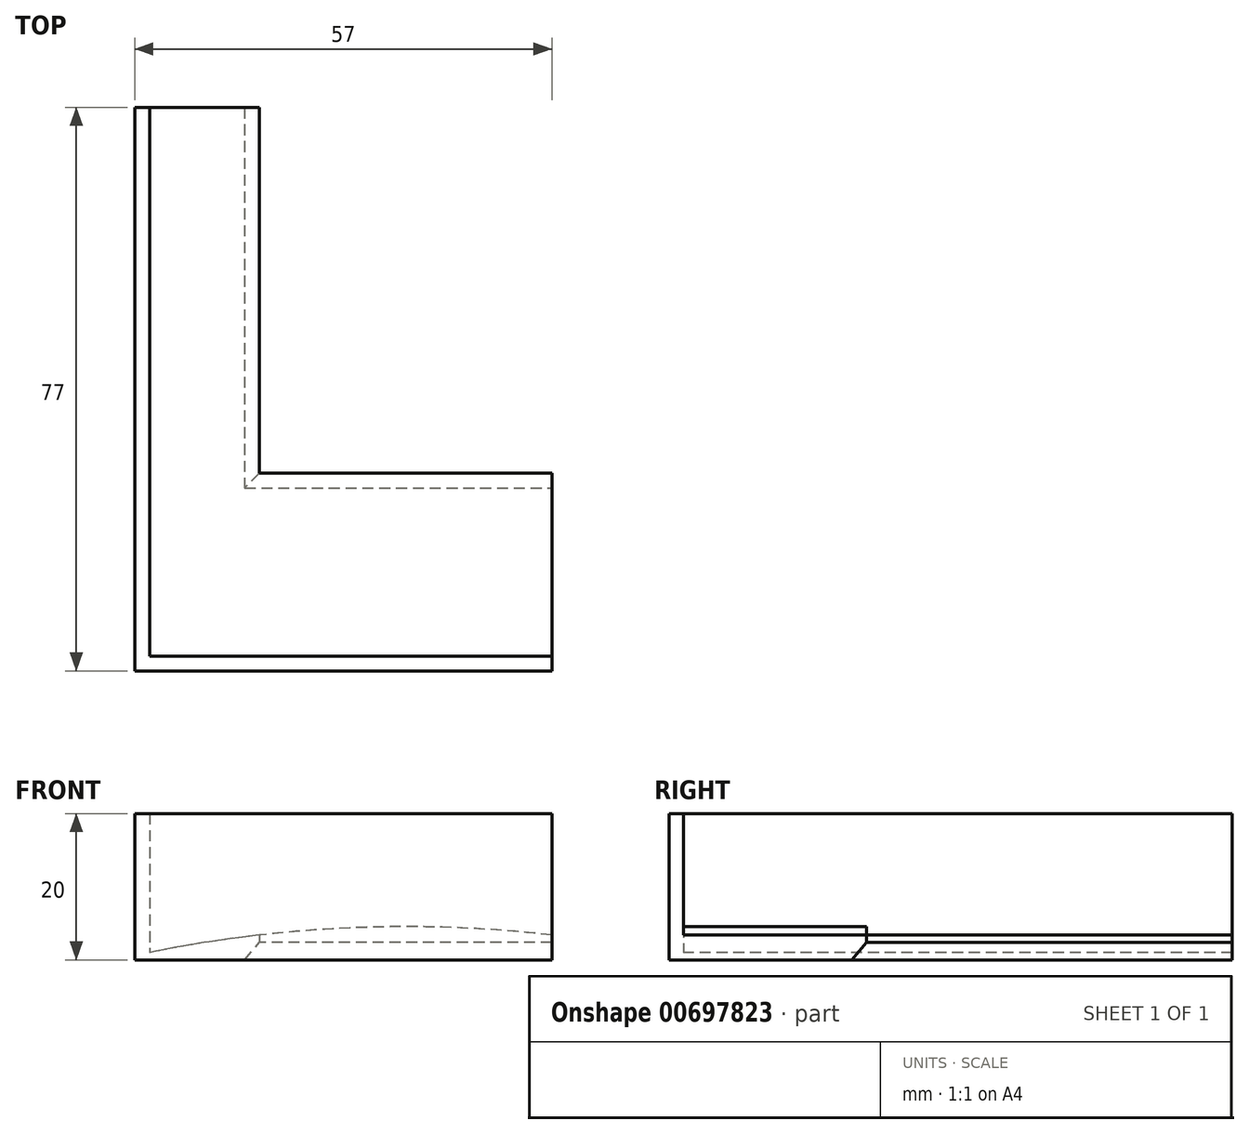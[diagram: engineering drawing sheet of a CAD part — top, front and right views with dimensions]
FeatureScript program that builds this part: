
annotation { "Feature Type Name" : "Feature", "Feature Type Description" : "" }
export const myFeature = defineFeature(function(context is Context, id is Id, definition is map)
    precondition{}
    {
        {
            var Q0;
            Q0=qCreatedBy(makeId("Top.planeOp"),FACE);
            var sketch = newSketch(context, id + "F0", { "sketchPlane" : qUnion([Q0])});
            skLineSegment(sketch, "E0.top", {"start": v(0, 50) * mm, "end": v(-15, 50) * mm});
            skLineSegment(sketch, "E0.left", {"start": v(0, 0) * mm, "end": v(0, 50) * mm});
            skLineSegment(sketch, "E1.bottom", {"start": v(0, 0) * mm, "end": v(40, 0) * mm});
            skLineSegment(sketch, "E1.top", {"start": v(-15, -25) * mm, "end": v(40, -25) * mm});
            skLineSegment(sketch, "E1.right", {"start": v(40, 0) * mm, "end": v(40, -25) * mm});
            skLineSegment(sketch, "E2", {"start": v(-15, 50) * mm, "end": v(-15, -25) * mm});
            skSolve(sketch);
        }
        {
            var Q0;
            Q0=makeQuery(id+"F0.imprint","IMPRINT",FACE,{"disambiguationData":[TD([[makeQuery(id+"F0.imprint","IMPRINT",EDGE,{"derivedFrom":sQuery(id+"F0.wireOp",EDGE,"E0.top")}),1.0]])]});
            extrude(context, id + "F1", {"entities" : qUnion([Q0]), "depth" : 5 * mm, "offsetDistance" : 25 * mm});
        }
        {
            var Q0;
            Q0=makeQuery(id+"F1.opExtrude","SWEPT_FACE",FACE,{"disambiguationData":[OSD([sQuery(id+"F0.wireOp",EDGE,"E1.top")])]});
            var sketch = newSketch(context, id + "F2", { "sketchPlane" : qUnion([Q0])});
            skArc(sketch, "E3", {"start": v(55, 1) * mm, "mid": v(20, 4.54) * mm, "end": v(-15, 1) * mm});
            skLineSegment(sketch, "E4", {"start": v(-15, 1) * mm, "end": v(-15, 13) * mm});
            skLineSegment(sketch, "E5", {"start": v(-15, 13) * mm, "end": v(55, 13) * mm});
            skLineSegment(sketch, "E6", {"start": v(55, 13) * mm, "end": v(55, 1) * mm});
            skSolve(sketch);
        }
        {
            var Q0;
            {var subQ2=sQuery(id+"F0.wireOp",EDGE,"E1.top");var subQ6=makeQuery(id+"F1.opExtrude","CAP_EDGE",EDGE,{"disambiguationData":[OSD([subQ2])],"isStart":false});Q0=makeQuery(id+"F2.imprint","IMPRINT",FACE,{"disambiguationData":[TD([[makeQuery(id+"F2.imprint","IMPRINT",EDGE,{"derivedFrom":subQ6}),-1.0]])]});}
            extrude(context, id + "F3", {"entities" : qUnion([Q0]), "operationType" : NewBodyOperationType.REMOVE, "oppositeDirection" : true, "depth" : 80 * mm, "offsetDistance" : 25 * mm});
        }
        {
            var Q0;
            Q0=makeQuery(id+"F1.opExtrude","CAP_FACE",FACE,{"disambiguationData":[OSD([sQuery(id+"F0.wireOp",EDGE,"E0.top"),sQuery(id+"F0.wireOp",EDGE,"E0.left"),sQuery(id+"F0.wireOp",EDGE,"E1.bottom"),sQuery(id+"F0.wireOp",EDGE,"E1.top"),sQuery(id+"F0.wireOp",EDGE,"E1.right"),sQuery(id+"F0.wireOp",EDGE,"E2")])],"isStart":true});
            var sketch = newSketch(context, id + "F4", { "sketchPlane" : qUnion([Q0])});
            skLineSegment(sketch, "E7.bottom", {"start": v(-15, -50) * mm, "end": v(-17, -50) * mm});
            skLineSegment(sketch, "E7.left", {"start": v(-15, -50) * mm, "end": v(-15, 25) * mm});
            skLineSegment(sketch, "E8.bottom", {"start": v(-15, 25) * mm, "end": v(40, 25) * mm});
            skLineSegment(sketch, "E8.top", {"start": v(-17, 27) * mm, "end": v(40, 27) * mm});
            skLineSegment(sketch, "E8.right", {"start": v(40, 25) * mm, "end": v(40, 27) * mm});
            skLineSegment(sketch, "E9", {"start": v(-17, 27) * mm, "end": v(-17, -50) * mm});
            skSolve(sketch);
        }
        {
            var Q0;
            Q0=makeQuery(id+"F4.imprint","IMPRINT",FACE,{"disambiguationData":[TD([[makeQuery(id+"F4.imprint","IMPRINT",EDGE,{"derivedFrom":sQuery(id+"F4.wireOp",EDGE,"E7.bottom")}),-1.0]])]});
            extrude(context, id + "F5", {"entities" : qUnion([Q0]), "operationType" : NewBodyOperationType.ADD, "oppositeDirection" : true, "depth" : 20 * mm, "offsetDistance" : 25 * mm});
        }
        {
            var Q0;
            Q0=makeQuery(id+"F1.opExtrude","CAP_EDGE",EDGE,{"disambiguationData":[OSD([sQuery(id+"F0.wireOp",EDGE,"E1.bottom")])],"isStart":true});
            var Q1;
            Q1=makeQuery(id+"F1.opExtrude","CAP_EDGE",EDGE,{"disambiguationData":[OSD([sQuery(id+"F0.wireOp",EDGE,"E0.left")])],"isStart":true});
            chamfer(context, id + "F6", {"entities" : qUnion([Q0, Q1]), "chamferType" : ChamferType.OFFSET_ANGLE, "width" : 2 * mm, "oppositeDirection" : false, "angle" : 50 * degree, "tangentPropagation" : true});
        }
    });
